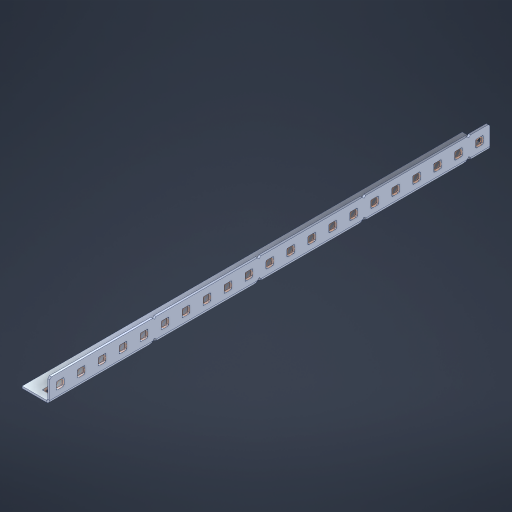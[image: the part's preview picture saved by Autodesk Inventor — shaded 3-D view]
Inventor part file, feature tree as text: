
AUTODESK INVENTOR PART (.ipt)
format: ipt  version: 2023 (Build 270158000, 158)  size: 782,848 bytes
history: native  units: in
note: dims shown in document units (in); Inventor stores cm internally (conversion verified against a paired STEP export)
features: other x47, extrude x41, sheet_metal_op x10, sketch x8, mirror x1, pattern_linear x1, chamfer x1
ambient origin geometry x8: Origin, YZ Plane, XZ Plane, XY Plane, X Axis, Y Axis, Z Axis, Center Point
bodies: Solid1 (feature_tree), Body (feature_tree)
feature tree (109):
  other  "Flange Pattern Plane"
  sheet_metal_op  "Flange Pattern"
  sheet_metal_op  "Body Pattern"
  other  "Arc Length"
  mirror  "Notch Mirror"
  pattern_linear  "Notch Pattern"  Spacing1=0.1875in  [1 undecoded]
  chamfer  "End Chamfer"
  extrude  "Half Cut"  Depth=0.0469in
  sketch  "Sketch1"  dims[d0=2.5in]
  other  "Plate1"
  sketch  "Sketch2"  dims[d1=10.5in]
  other  "Plate2"
  sheet_metal_op  "Bend1"
  sheet_metal_op  "Corner1"
  sketch  "Sketch3"  dims[d2=0.0469in]
  other  "Flange Pattern Sketch"
  sketch  "Sketch7"  dims[d3=0.0469in]
  other  "Srf1"
  other  "Srf2"
  sketch  "Sketch8"  dims[d4=0.0234in]
  sketch  "Sketch9"  dims[d5=0.0938in]
  other  "Srf91"
  sheet_metal_op  "Body Pattern Sketch"
  other  "Srf92"
  sketch  "Sketch13"  dims[d6=0.0469in]
  sketch  "Sketch14"  dims[d7=0.5in d8=90.0deg d9=0.0312in d10=0.1875in d11=0.0469in d12=0.0469in d16=0.182in d17=0.02in d18=0.0469in d19=0.0in d20=0.25in d21=0.25in d46=0.172in d47=1.0in d48=0.0in d49=0.182in d50=0.02in d51=0.25in d52=0.25in d53=0.0469in d54=0.0in d55=0.172in d56=1.0in d57=0.0in d60=8.2677in d62=0.5in d63=0.3937in d65=0.5in d85=0.1227in d86=0.1659in d88=0.04in d89=0.0469in d90=0.0in d91=0.04in d92=0.0491in d95=2.5in d96=0.04in d97=0.25in d98=45.0deg d101=0.0in d102=2.497in d131=0.5in d132=8.2677in d134=0.5in d139=0.5in]
  other  "Srf856"
  other  "Srf1310"
  other  "Srf1311"
  other  "Srf1312"
  other  "Srf1376"
  other  "Srf1377"
  other  "Srf1728"
  other  "Srf1755"
  other  "Srf1878"
  other  "Srf1879"
  other  "Srf1880"
  other  "Srf1881"
  other  "Srf1882"
  other  "Srf1883"
  other  "Srf1884"
  other  "Srf1885"
  other  "Srf1886"
  other  "Srf1887"
  other  "Srf1888"
  other  "Srf1889"
  other  "Srf1890"
  other  "Srf1891"
  other  "Srf1892"
  other  "Srf1942"
  other  "Srf1943"
  other  "Srf1944"
  other  "Srf1945"
  other  "Srf1946"
  other  "Srf1947"
  other  "Srf1948"
  other  "Srf1949"
  other  "Srf1950"
  other  "Srf1951"
  other  "Srf1952"
  other  "Srf1953"
  other  "Srf1954"
  other  "Srf1955"
  other  "Srf1956"
  sheet_metal_op  "Flange Stamp"
  sheet_metal_op  "Flange Circle"
  sheet_metal_op  "Body Stamp"
  sheet_metal_op  "Body Circle"
  sheet_metal_op  "Notch"
  extrude  "ExtrusionSrf2"  Depth=0.0469in
  extrude  "ExtrusionSrf92"  Depth=0.5in
  extrude  "ExtrusionSrf856"  Depth=0.02in
  extrude  "ExtrusionSrf1310"  Depth=0.0469in
  extrude  "ExtrusionSrf1311"  TaperAngle=0.0deg  [1 undecoded]
  extrude  "ExtrusionSrf1312"  Depth=0.5in
  extrude  "ExtrusionSrf1376"  Depth=0.5in
  extrude  "ExtrusionSrf1377"  Depth=0.5in
  extrude  "ExtrusionSrf1728"  Depth=0.5in TaperAngle=0.0deg
  extrude  "ExtrusionSrf1755"  Depth=0.5in
  extrude  "ExtrusionSrf1878"  Depth=0.02in
  extrude  "ExtrusionSrf1879"  Depth=0.5in
  extrude  "ExtrusionSrf1880"  Depth=0.5in
  extrude  "ExtrusionSrf1881"  Depth=0.0469in
  extrude  "ExtrusionSrf1882"  TaperAngle=0.0deg  [1 undecoded]
  extrude  "ExtrusionSrf1883"  Depth=0.5in
  extrude  "ExtrusionSrf1884"  Depth=0.5in TaperAngle=0.0deg
  extrude  "ExtrusionSrf1885"  Depth=0.5in
  extrude  "ExtrusionSrf1886"  Depth=0.5in
  extrude  "ExtrusionSrf1887"  Depth=0.5in
  extrude  "ExtrusionSrf1888"  Depth=0.5in
  extrude  "ExtrusionSrf1889"  Depth=0.5in
  extrude  "ExtrusionSrf1890"  Depth=0.0469in
  extrude  "ExtrusionSrf1891"  TaperAngle=0.0deg  [1 undecoded]
  extrude  "ExtrusionSrf1892"  Depth=0.5in
  extrude  "ExtrusionSrf1942"  Depth=0.5in
  extrude  "ExtrusionSrf1943"  Depth=0.5in
  extrude  "ExtrusionSrf1944"  Depth=0.5in TaperAngle=45.0deg
  extrude  "ExtrusionSrf1945"  TaperAngle=0.0deg  [1 undecoded]
  extrude  "ExtrusionSrf1946"  Depth=0.5in
  extrude  "ExtrusionSrf1947"  Depth=0.5in
  extrude  "ExtrusionSrf1948"  Depth=0.5in
  extrude  "ExtrusionSrf1949"  Depth=0.5in
  extrude  "ExtrusionSrf1950"  Depth=0.5in
  extrude  "ExtrusionSrf1951"  [1 undecoded]
  extrude  "ExtrusionSrf1952"  [1 undecoded]
  extrude  "ExtrusionSrf1953"  [1 undecoded]
  extrude  "ExtrusionSrf1954"  [1 undecoded]
  extrude  "ExtrusionSrf1955"  [1 undecoded]
  extrude  "ExtrusionSrf1956"  [1 undecoded]
note: 11 required parameter values undecoded (feature->parameter linkage not recoverable at this tier; creation-order binding heuristic only, values carry confidence <= 0.55)
